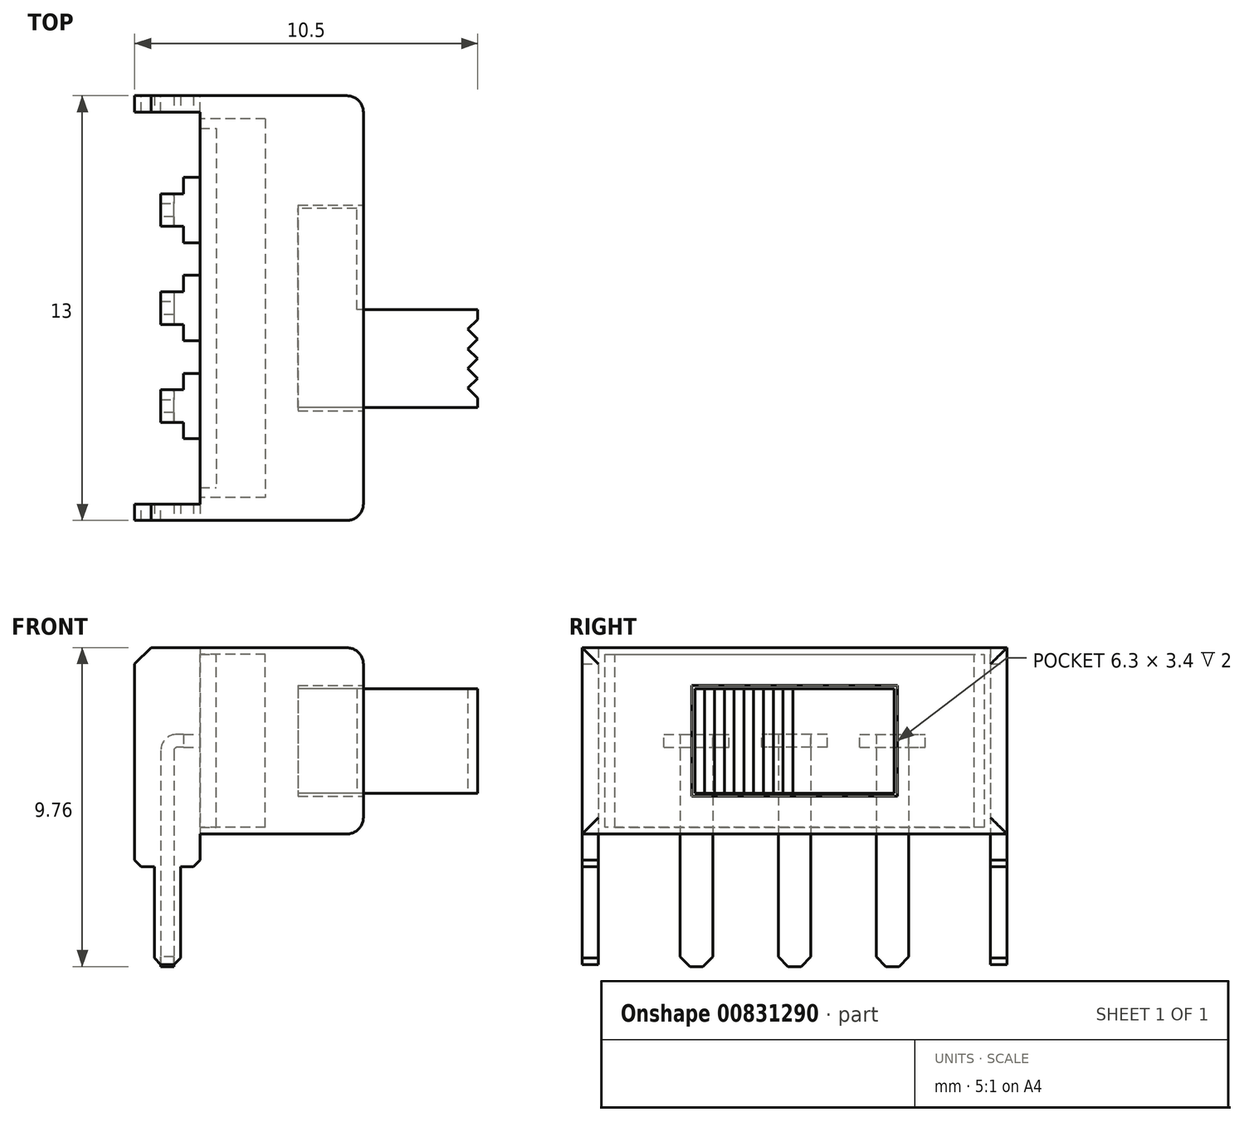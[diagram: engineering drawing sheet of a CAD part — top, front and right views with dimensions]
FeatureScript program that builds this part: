
annotation { "Feature Type Name" : "Feature", "Feature Type Description" : "" }
export const myFeature = defineFeature(function(context is Context, id is Id, definition is map)
    precondition{}
    {
        {
            var Q0;
            Q0=qCreatedBy(makeId("Top.planeOp"),FACE);
            var sketch = newSketch(context, id + "F0", { "sketchPlane" : qUnion([Q0])});
            skLineSegment(sketch, "E0.bottom", {"start": v(2.5, 6.5) * mm, "end": v(-2.5, 6.5) * mm});
            skLineSegment(sketch, "E0.top", {"start": v(2.5, -6.5) * mm, "end": v(-2.5, -6.5) * mm});
            skLineSegment(sketch, "E0.left", {"start": v(2.5, 6.5) * mm, "end": v(2.5, -6.5) * mm});
            skLineSegment(sketch, "E0.right", {"start": v(-2.5, 6.5) * mm, "end": v(-2.5, -6.5) * mm});
            skPoint(sketch, "E0.middle", {"position": v(0, 0) * mm});
            skSolve(sketch);
        }
        {
            var Q0;
            Q0 = qSketchRegion(id + "F0", true);
            extrude(context, id + "F1", {"entities" : qUnion([Q0]), "depth" : 5.7 * mm, "offsetDistance" : 25 * mm});
        }
        {
            var Q0;
            Q0=makeQuery(id+"F1.opExtrude","SWEPT_FACE",FACE,{"disambiguationData":[OSD([sQuery(id+"F0.wireOp",EDGE,"E0.left")])]});
            var sketch = newSketch(context, id + "F2", { "sketchPlane" : qUnion([Q0])});
            skLineSegment(sketch, "E1.bottom", {"start": v(3.15, 4.55) * mm, "end": v(-3.15, 4.55) * mm});
            skLineSegment(sketch, "E1.top", {"start": v(3.15, 1.15) * mm, "end": v(-3.15, 1.15) * mm});
            skLineSegment(sketch, "E1.left", {"start": v(3.15, 4.55) * mm, "end": v(3.15, 1.15) * mm});
            skLineSegment(sketch, "E1.right", {"start": v(-3.15, 4.55) * mm, "end": v(-3.15, 1.15) * mm});
            skPoint(sketch, "E1.middle", {"position": v(0, 2.85) * mm});
            skPoint(sketch, "E1.middle.positionSnap0", {"position": v(-6.5, 2.85) * mm});
            skPoint(sketch, "E1.middle.positionSnap1", {"position": v(0, 5.7) * mm});
            skPoint(sketch, "E1.centerSnap0", {"position": v(-6.5, 2.85) * mm});
            skPoint(sketch, "E1.centerSnap1", {"position": v(0, 5.7) * mm});
            skSolve(sketch);
        }
        {
            var Q0;
            Q0 = qSketchRegion(id + "F2", true);
            extrude(context, id + "F3", {"entities" : qUnion([Q0]), "operationType" : NewBodyOperationType.REMOVE, "oppositeDirection" : true, "depth" : 2 * mm, "offsetDistance" : 25 * mm});
        }
        {
            var Q0;
            Q0=makeQuery(id+"F3.boolean.opBoolean","COPY",FACE,{"derivedFrom":makeQuery(id+"F3.opExtrude","CAP_FACE",FACE,{"disambiguationData":[OSD([sQuery(id+"F2.wireOp",EDGE,"E1.bottom"),sQuery(id+"F2.wireOp",EDGE,"E1.top"),sQuery(id+"F2.wireOp",EDGE,"E1.left"),sQuery(id+"F2.wireOp",EDGE,"E1.right")])],"isStart":false})});
            var sketch = newSketch(context, id + "F4", { "sketchPlane" : qUnion([Q0])});
            skLineSegment(sketch, "E2.0", {"start": v(-3.05, 1.25) * mm, "end": v(3.05, 1.25) * mm});
            skLineSegment(sketch, "E2.1", {"start": v(-3.05, 4.45) * mm, "end": v(-3.05, 1.25) * mm});
            skLineSegment(sketch, "E2.2", {"start": v(3.05, 4.45) * mm, "end": v(-3.05, 4.45) * mm});
            skLineSegment(sketch, "E2.3", {"start": v(3.05, 1.25) * mm, "end": v(3.05, 4.45) * mm});
            skSolve(sketch);
        }
        {
            var Q0;
            Q0=makeQuery(id+"F4.imprint","IMPRINT",FACE,{"disambiguationData":[TD([[makeQuery(id+"F4.imprint","IMPRINT",EDGE,{"derivedFrom":sQuery(id+"F4.wireOp",EDGE,"E2.0")}),1.0]])]});
            extrude(context, id + "F5", {"entities" : qUnion([Q0]), "depth" : 1.8 * mm, "offsetDistance" : 25 * mm});
        }
        {
            var Q0;
            Q0=makeQuery(id+"F5.opExtrude","CAP_FACE",FACE,{"disambiguationData":[OSD([sQuery(id+"F4.wireOp",EDGE,"E2.0"),sQuery(id+"F4.wireOp",EDGE,"E2.1"),sQuery(id+"F4.wireOp",EDGE,"E2.2"),sQuery(id+"F4.wireOp",EDGE,"E2.3")])],"isStart":false});
            var sketch = newSketch(context, id + "F6", { "sketchPlane" : qUnion([Q0])});
            skLineSegment(sketch, "E3", {"start": v(-0.05, 4.45) * mm, "end": v(-0.05, 1.25) * mm});
            skSolve(sketch);
        }
        {
            var Q0;
            Q0 = qSketchRegion(id + "F6", true);
            var Q1;
            {var subQ0=sQuery(id+"F6.wireOp",EDGE,"E3");Q1=makeQuery(id+"F6.imprint","IMPRINT",FACE,{"disambiguationData":[TD([[makeQuery(id+"F6.imprint","IMPRINT",EDGE,{"derivedFrom":subQ0}),-1.0]])]});}
            extrude(context, id + "F7", {"entities" : qUnion([Q0, Q1]), "operationType" : NewBodyOperationType.ADD, "depth" : 3.7 * mm, "offsetDistance" : 25 * mm});
        }
        {
            var Q0;
            Q0=makeQuery(id+"F1.opExtrude","SWEPT_FACE",FACE,{"disambiguationData":[OSD([sQuery(id+"F0.wireOp",EDGE,"E0.right")])]});
            var sketch = newSketch(context, id + "F8", { "sketchPlane" : qUnion([Q0])});
            skLineSegment(sketch, "E4", {"start": v(-6, 5.7) * mm, "end": v(-6, 0) * mm});
            skLineSegment(sketch, "E5", {"start": v(6, 5.7) * mm, "end": v(6, 0) * mm});
            skSolve(sketch);
        }
        {
            var Q0;
            Q0 = qSketchRegion(id + "F8", true);
            var Q1;
            {var subQ0=sQuery(id+"F8.wireOp",EDGE,"E4");Q1=makeQuery(id+"F8.imprint","IMPRINT",FACE,{"disambiguationData":[TD([[makeQuery(id+"F8.imprint","IMPRINT",EDGE,{"derivedFrom":subQ0}),-1.0]])]});}
            var Q2;
            {var subQ0=sQuery(id+"F8.wireOp",EDGE,"E5");Q2=makeQuery(id+"F8.imprint","IMPRINT",FACE,{"disambiguationData":[TD([[makeQuery(id+"F8.imprint","IMPRINT",EDGE,{"derivedFrom":subQ0}),1.0]])]});}
            extrude(context, id + "F9", {"entities" : qUnion([Q0, Q1, Q2]), "operationType" : NewBodyOperationType.ADD, "depth" : 2 * mm, "offsetDistance" : 25 * mm});
        }
        {
            var Q0;
            {var subQ0=sQuery(id+"F0.wireOp",EDGE,"E0.right");var subQ1=makeQuery(id+"F1.opExtrude","CAP_EDGE",EDGE,{"disambiguationData":[OSD([subQ0])],"isStart":true});var subQ2=sQuery(id+"F0.wireOp",EDGE,"E0.top");var subQ3=sQuery(id+"F0.wireOp",EDGE,"E0.bottom");Q0=makeQuery(id+"F9.boolean.opBoolean","MERGE",FACE,{"derivedFrom":[makeQuery(id+"F1.opExtrude","CAP_FACE",FACE,{"disambiguationData":[OSD([subQ3,subQ2,sQuery(id+"F0.wireOp",EDGE,"E0.left"),subQ0])],"isStart":true}),makeQuery(id+"F9.opExtrude","SWEPT_FACE",FACE,{"disambiguationData":[OSD([subQ0]),TDD([makeQuery(id+"F8.imprint","IMPRINT",EDGE,{"disambiguationData":[TD([[makeQuery(id+"F8.imprint","INTERSECT",VERTEX,{"derivedFrom":[subQ1,sQuery(id+"F8.wireOp",EDGE,"E4")]}),1.0]])],"derivedFrom":subQ1})])]}),makeQuery(id+"F9.opExtrude","SWEPT_FACE",FACE,{"disambiguationData":[OSD([subQ0]),TDD([makeQuery(id+"F8.imprint","IMPRINT",EDGE,{"disambiguationData":[TD([[makeQuery(id+"F8.imprint","INTERSECT",VERTEX,{"derivedFrom":[subQ1,sQuery(id+"F8.wireOp",EDGE,"E5")]}),-1.0]])],"derivedFrom":subQ1})])]})]});}
            var sketch = newSketch(context, id + "F10", { "sketchPlane" : qUnion([Q0])});
            skLineSegment(sketch, "E6", {"start": v(-2.5, -6) * mm, "end": v(-2.5, -6.5) * mm});
            skLineSegment(sketch, "E7", {"start": v(-2.5, 6) * mm, "end": v(-2.5, 6.5) * mm});
            skSolve(sketch);
        }
        {
            var Q0;
            Q0 = qSketchRegion(id + "F10", true);
            var Q1;
            {var subQ0=sQuery(id+"F10.wireOp",EDGE,"E7");Q1=makeQuery(id+"F10.imprint","IMPRINT",FACE,{"disambiguationData":[TD([[makeQuery(id+"F10.imprint","IMPRINT",EDGE,{"derivedFrom":subQ0}),1.0]])]});}
            var Q2;
            {var subQ0=sQuery(id+"F10.wireOp",EDGE,"E6");Q2=makeQuery(id+"F10.imprint","IMPRINT",FACE,{"disambiguationData":[TD([[makeQuery(id+"F10.imprint","IMPRINT",EDGE,{"derivedFrom":subQ0}),-1.0]])]});}
            extrude(context, id + "F11", {"entities" : qUnion([Q0, Q1, Q2]), "operationType" : NewBodyOperationType.ADD, "depth" : 1 * mm, "offsetDistance" : 25 * mm});
        }
        {
            var Q0;
            Q0=makeQuery(id+"F11.opExtrude","CAP_FACE",FACE,{"disambiguationData":[OSD([sQuery(id+"F0.wireOp",EDGE,"E0.bottom"),sQuery(id+"F0.wireOp",EDGE,"E0.right"),sQuery(id+"F8.wireOp",EDGE,"E4"),sQuery(id+"F10.wireOp",EDGE,"E6")])],"isStart":false});
            var sketch = newSketch(context, id + "F12", { "sketchPlane" : qUnion([Q0])});
            skLineSegment(sketch, "E8", {"start": v(-3.1, -6.5) * mm, "end": v(-3.1, -6) * mm});
            skLineSegment(sketch, "E9", {"start": v(-3.9, -6.5) * mm, "end": v(-3.9, -6) * mm});
            skSolve(sketch);
        }
        {
            var Q0;
            Q0 = qSketchRegion(id + "F12", true);
            var Q1;
            {var subQ0=sQuery(id+"F12.wireOp",EDGE,"E8");Q1=makeQuery(id+"F12.imprint","IMPRINT",FACE,{"disambiguationData":[TD([[makeQuery(id+"F12.imprint","IMPRINT",EDGE,{"derivedFrom":subQ0}),1.0]])]});}
            extrude(context, id + "F13", {"entities" : qUnion([Q0, Q1]), "operationType" : NewBodyOperationType.ADD, "depth" : 3 * mm, "offsetDistance" : 25 * mm});
        }
        {
            var Q0;
            Q0=makeQuery(id+"F11.opExtrude","CAP_FACE",FACE,{"disambiguationData":[OSD([sQuery(id+"F0.wireOp",EDGE,"E0.top"),sQuery(id+"F0.wireOp",EDGE,"E0.right"),sQuery(id+"F8.wireOp",EDGE,"E5"),sQuery(id+"F10.wireOp",EDGE,"E7")])],"isStart":false});
            var sketch = newSketch(context, id + "F14", { "sketchPlane" : qUnion([Q0])});
            skLineSegment(sketch, "E10", {"start": v(-3.1, 6) * mm, "end": v(-3.1, 6.5) * mm});
            skLineSegment(sketch, "E11", {"start": v(-3.9, 6) * mm, "end": v(-3.9, 6.5) * mm});
            skSolve(sketch);
        }
        {
            var Q0;
            Q0 = qSketchRegion(id + "F14", true);
            var Q1;
            {var subQ0=sQuery(id+"F14.wireOp",EDGE,"E10");Q1=makeQuery(id+"F14.imprint","IMPRINT",FACE,{"disambiguationData":[TD([[makeQuery(id+"F14.imprint","IMPRINT",EDGE,{"derivedFrom":subQ0}),1.0]])]});}
            extrude(context, id + "F15", {"entities" : qUnion([Q0, Q1]), "operationType" : NewBodyOperationType.ADD, "depth" : 3 * mm, "offsetDistance" : 25 * mm});
        }
        {
            var Q0;
            Q0=makeQuery(id+"F13.opExtrude","CAP_EDGE",EDGE,{"disambiguationData":[OSD([sQuery(id+"F12.wireOp",EDGE,"E9")])],"isStart":false});
            var Q1;
            Q1=makeQuery(id+"F13.opExtrude","CAP_EDGE",EDGE,{"disambiguationData":[OSD([sQuery(id+"F12.wireOp",EDGE,"E8")])],"isStart":false});
            var Q2;
            Q2=makeQuery(id+"F15.opExtrude","CAP_EDGE",EDGE,{"disambiguationData":[OSD([sQuery(id+"F14.wireOp",EDGE,"E11")])],"isStart":false});
            var Q3;
            Q3=makeQuery(id+"F15.opExtrude","CAP_EDGE",EDGE,{"disambiguationData":[OSD([sQuery(id+"F14.wireOp",EDGE,"E10")])],"isStart":false});
            chamfer(context, id + "F16", {"entities" : qUnion([Q0, Q1, Q2, Q3]), "width" : 0.2 * mm, "tangentPropagation" : true});
        }
        {
            var Q0;
            {var subQ0=sQuery(id+"F0.wireOp",EDGE,"E0.right");var subQ1=makeQuery(id+"F1.opExtrude","CAP_EDGE",EDGE,{"disambiguationData":[OSD([subQ0])],"isStart":true});Q0=makeQuery(id+"F11.opExtrude","CAP_EDGE",EDGE,{"disambiguationData":[OSD([subQ0]),TDD([makeQuery(id+"F10.imprint","IMPRINT",EDGE,{"derivedFrom":makeQuery(id+"F9.opExtrude","CAP_EDGE",EDGE,{"disambiguationData":[OSD([subQ0]),TDD([makeQuery(id+"F8.imprint","IMPRINT",EDGE,{"disambiguationData":[TD([[makeQuery(id+"F8.imprint","INTERSECT",VERTEX,{"derivedFrom":[subQ1,sQuery(id+"F8.wireOp",EDGE,"E4")]}),1.0]])],"derivedFrom":subQ1})])],"isStart":false})})])],"isStart":false});}
            var Q1;
            Q1=makeQuery(id+"F11.opExtrude","CAP_EDGE",EDGE,{"disambiguationData":[OSD([sQuery(id+"F10.wireOp",EDGE,"E6")])],"isStart":false});
            var Q2;
            {var subQ0=sQuery(id+"F0.wireOp",EDGE,"E0.right");var subQ1=makeQuery(id+"F1.opExtrude","CAP_EDGE",EDGE,{"disambiguationData":[OSD([subQ0])],"isStart":true});Q2=makeQuery(id+"F11.opExtrude","CAP_EDGE",EDGE,{"disambiguationData":[OSD([subQ0]),TDD([makeQuery(id+"F10.imprint","IMPRINT",EDGE,{"derivedFrom":makeQuery(id+"F9.opExtrude","CAP_EDGE",EDGE,{"disambiguationData":[OSD([subQ0]),TDD([makeQuery(id+"F8.imprint","IMPRINT",EDGE,{"disambiguationData":[TD([[makeQuery(id+"F8.imprint","INTERSECT",VERTEX,{"derivedFrom":[subQ1,sQuery(id+"F8.wireOp",EDGE,"E5")]}),-1.0]])],"derivedFrom":subQ1})])],"isStart":false})})])],"isStart":false});}
            var Q3;
            Q3=makeQuery(id+"F11.opExtrude","CAP_EDGE",EDGE,{"disambiguationData":[OSD([sQuery(id+"F10.wireOp",EDGE,"E7")])],"isStart":false});
            chamfer(context, id + "F17", {"entities" : qUnion([Q0, Q1, Q2, Q3]), "width" : 0.2 * mm, "tangentPropagation" : true});
        }
        {
            var Q0;
            Q0=makeQuery(id+"F1.opExtrude","CAP_EDGE",EDGE,{"disambiguationData":[OSD([sQuery(id+"F0.wireOp",EDGE,"E0.left")])],"isStart":false});
            var Q1;
            Q1=makeQuery(id+"F1.opExtrude","SWEPT_EDGE",EDGE,{"disambiguationData":[OSD([sQuery(id+"F0.wireOp",EDGE,"E0.bottom"),sQuery(id+"F0.wireOp",EDGE,"E0.left")])]});
            var Q2;
            Q2=makeQuery(id+"F1.opExtrude","CAP_EDGE",EDGE,{"disambiguationData":[OSD([sQuery(id+"F0.wireOp",EDGE,"E0.left")])],"isStart":true});
            var Q3;
            Q3=makeQuery(id+"F1.opExtrude","SWEPT_EDGE",EDGE,{"disambiguationData":[OSD([sQuery(id+"F0.wireOp",EDGE,"E0.top"),sQuery(id+"F0.wireOp",EDGE,"E0.left")])]});
            fillet(context, id + "F18", {"entities" : qUnion([Q0, Q1, Q2, Q3]), "radius" : 0.5 * mm, "tangentPropagation" : true, "allowEdgeOverflow" : false});
        }
        {
            var Q0;
            {var subQ0=sQuery(id+"F0.wireOp",EDGE,"E0.right");var subQ1=makeQuery(id+"F1.opExtrude","CAP_EDGE",EDGE,{"disambiguationData":[OSD([subQ0])],"isStart":false});Q0=makeQuery(id+"F9.opExtrude","CAP_EDGE",EDGE,{"disambiguationData":[OSD([subQ0]),TDD([makeQuery(id+"F8.imprint","IMPRINT",EDGE,{"disambiguationData":[TD([[makeQuery(id+"F8.imprint","INTERSECT",VERTEX,{"derivedFrom":[subQ1,sQuery(id+"F8.wireOp",EDGE,"E4")]}),1.0]])],"derivedFrom":subQ1})])],"isStart":false});}
            var Q1;
            {var subQ0=sQuery(id+"F0.wireOp",EDGE,"E0.right");var subQ1=makeQuery(id+"F1.opExtrude","CAP_EDGE",EDGE,{"disambiguationData":[OSD([subQ0])],"isStart":false});Q1=makeQuery(id+"F9.opExtrude","CAP_EDGE",EDGE,{"disambiguationData":[OSD([subQ0]),TDD([makeQuery(id+"F8.imprint","IMPRINT",EDGE,{"disambiguationData":[TD([[makeQuery(id+"F8.imprint","INTERSECT",VERTEX,{"derivedFrom":[subQ1,sQuery(id+"F8.wireOp",EDGE,"E5")]}),-1.0]])],"derivedFrom":subQ1})])],"isStart":false});}
            chamfer(context, id + "F19", {"entities" : qUnion([Q0, Q1]), "width" : 0.5 * mm, "tangentPropagation" : true});
        }
        {
            var Q0;
            Q0=makeQuery(id+"F1.opExtrude","SWEPT_FACE",FACE,{"disambiguationData":[OSD([sQuery(id+"F0.wireOp",EDGE,"E0.right")])]});
            var sketch = newSketch(context, id + "F20", { "sketchPlane" : qUnion([Q0])});
            skLineSegment(sketch, "E12.0", {"start": v(5.8, 0.2) * mm, "end": v(5.8, 5.5) * mm});
            skLineSegment(sketch, "E12.1", {"start": v(-5.8, 0.2) * mm, "end": v(5.8, 0.2) * mm});
            skLineSegment(sketch, "E12.2", {"start": v(-5.8, 5.5) * mm, "end": v(-5.8, 0.2) * mm});
            skLineSegment(sketch, "E12.3", {"start": v(5.8, 5.5) * mm, "end": v(-5.8, 5.5) * mm});
            skSolve(sketch);
        }
        {
            var Q0;
            Q0 = qSketchRegion(id + "F20", true);
            extrude(context, id + "F21", {"entities" : qUnion([Q0]), "operationType" : NewBodyOperationType.REMOVE, "oppositeDirection" : true, "depth" : 2 * mm, "offsetDistance" : 25 * mm});
        }
        {
            var Q0;
            Q0=makeQuery(id+"F21.boolean.opBoolean","COPY",FACE,{"derivedFrom":makeQuery(id+"F21.opExtrude","SWEPT_FACE",FACE,{"disambiguationData":[OSD([sQuery(id+"F20.wireOp",EDGE,"E12.3")])]})});
            var sketch = newSketch(context, id + "F22", { "sketchPlane" : qUnion([Q0])});
            skLineSegment(sketch, "E13.bottom", {"start": v(-2.5, -5.5) * mm, "end": v(-2, -5.5) * mm});
            skLineSegment(sketch, "E13.top", {"start": v(-2.5, 5.5) * mm, "end": v(-2, 5.5) * mm});
            skLineSegment(sketch, "E13.left", {"start": v(-2.5, -5.5) * mm, "end": v(-2.5, 5.5) * mm});
            skLineSegment(sketch, "E13.right", {"start": v(-2, -5.5) * mm, "end": v(-2, 5.5) * mm});
            skSolve(sketch);
        }
        {
            var Q0;
            Q0 = qSketchRegion(id + "F22", true);
            extrude(context, id + "F23", {"entities" : qUnion([Q0]), "depth" : 5.3 * mm, "offsetDistance" : 25 * mm});
        }
        {
            var Q0;
            Q0=makeQuery(id+"F23.opExtrude","SWEPT_FACE",FACE,{"disambiguationData":[OSD([sQuery(id+"F22.wireOp",EDGE,"E13.left")])]});
            var sketch = newSketch(context, id + "F24", { "sketchPlane" : qUnion([Q0])});
            skLineSegment(sketch, "E14.bottom", {"start": v(-2, 2.65) * mm, "end": v(-4, 2.65) * mm});
            skLineSegment(sketch, "E14.top", {"start": v(-2, 3.05) * mm, "end": v(-4, 3.05) * mm});
            skLineSegment(sketch, "E14.left", {"start": v(-2, 2.65) * mm, "end": v(-2, 3.05) * mm});
            skLineSegment(sketch, "E14.right", {"start": v(-4, 2.65) * mm, "end": v(-4, 3.05) * mm});
            skPoint(sketch, "E14.middle", {"position": v(-3, 2.85) * mm});
            skPoint(sketch, "E14.middle.positionSnap0", {"position": v(-5.5, 2.85) * mm});
            skPoint(sketch, "E14.centerSnap0", {"position": v(-5.5, 2.85) * mm});
            skLineSegment(sketch, "E15.bottom", {"start": v(-1, 2.65) * mm, "end": v(1, 2.65) * mm});
            skLineSegment(sketch, "E15.top", {"start": v(-1, 3.05) * mm, "end": v(1, 3.05) * mm});
            skLineSegment(sketch, "E15.left", {"start": v(-1, 2.65) * mm, "end": v(-1, 3.05) * mm});
            skLineSegment(sketch, "E15.right", {"start": v(1, 2.65) * mm, "end": v(1, 3.05) * mm});
            skPoint(sketch, "E15.middle", {"position": v(0, 2.85) * mm});
            skPoint(sketch, "E15.middle.positionSnap0", {"position": v(-2, 2.85) * mm});
            skPoint(sketch, "E15.middle.positionSnap1", {"position": v(0, 5.5) * mm});
            skPoint(sketch, "E15.centerSnap0", {"position": v(-2, 2.85) * mm});
            skPoint(sketch, "E15.centerSnap1", {"position": v(0, 5.5) * mm});
            skLineSegment(sketch, "E16.bottom", {"start": v(4, 2.65) * mm, "end": v(2, 2.65) * mm});
            skLineSegment(sketch, "E16.top", {"start": v(4, 3.05) * mm, "end": v(2, 3.05) * mm});
            skLineSegment(sketch, "E16.left", {"start": v(4, 2.65) * mm, "end": v(4, 3.05) * mm});
            skLineSegment(sketch, "E16.right", {"start": v(2, 2.65) * mm, "end": v(2, 3.05) * mm});
            skPoint(sketch, "E16.middle", {"position": v(3, 2.85) * mm});
            skSolve(sketch);
        }
        {
            var Q0;
            Q0=makeQuery(id+"F24.imprint","IMPRINT",FACE,{"disambiguationData":[TD([[makeQuery(id+"F24.imprint","IMPRINT",EDGE,{"derivedFrom":sQuery(id+"F24.wireOp",EDGE,"E15.bottom")}),1.0]])]});
            var Q1;
            Q1=makeQuery(id+"F24.imprint","IMPRINT",FACE,{"disambiguationData":[TD([[makeQuery(id+"F24.imprint","IMPRINT",EDGE,{"derivedFrom":sQuery(id+"F24.wireOp",EDGE,"E16.bottom")}),-1.0]])]});
            var Q2;
            Q2=makeQuery(id+"F24.imprint","IMPRINT",FACE,{"disambiguationData":[TD([[makeQuery(id+"F24.imprint","IMPRINT",EDGE,{"derivedFrom":sQuery(id+"F24.wireOp",EDGE,"E14.bottom")}),-1.0]])]});
            extrude(context, id + "F25", {"entities" : qUnion([Q0, Q1, Q2]), "depth" : 0.5 * mm, "offsetDistance" : 25 * mm});
        }
        {
            var Q0;
            Q0=makeQuery(id+"F25.opExtrude","CAP_FACE",FACE,{"disambiguationData":[OSD([sQuery(id+"F24.wireOp",EDGE,"E15.bottom"),sQuery(id+"F24.wireOp",EDGE,"E15.top"),sQuery(id+"F24.wireOp",EDGE,"E15.left"),sQuery(id+"F24.wireOp",EDGE,"E15.right")])],"isStart":false});
            var sketch = newSketch(context, id + "F26", { "sketchPlane" : qUnion([Q0])});
            skLineSegment(sketch, "E17", {"start": v(0.5, 3.05) * mm, "end": v(0.5, 2.65) * mm});
            skLineSegment(sketch, "E18", {"start": v(-0.5, 2.65) * mm, "end": v(-0.5, 3.05) * mm});
            skSolve(sketch);
        }
        {
            var Q0;
            Q0=makeQuery(id+"F25.opExtrude","SWEPT_FACE",FACE,{"disambiguationData":[OSD([sQuery(id+"F24.wireOp",EDGE,"E15.left")])]});
            var sketch = newSketch(context, id + "F27", { "sketchPlane" : qUnion([Q0])});
            skLineSegment(sketch, "E19", {"start": v(3.5, -4.06) * mm, "end": v(3.5, 2.55) * mm});
            skLineSegment(sketch, "E20", {"start": v(3.2, 2.85) * mm, "end": v(3, 2.85) * mm});
            skPoint(sketch, "E21.visualSharp", {"position": v(3.5, 2.85) * mm});
            skArc(sketch, "E21.filletArc", {"start": v(3.5, 2.55) * mm, "mid": v(3.41, 2.76) * mm, "end": v(3.2, 2.85) * mm});
            skSolve(sketch);
        }
        {
            var Q0;
            {var subQ0=sQuery(id+"F26.wireOp",EDGE,"E17");Q0=makeQuery(id+"F26.imprint","IMPRINT",FACE,{"disambiguationData":[TD([[makeQuery(id+"F26.imprint","IMPRINT",EDGE,{"derivedFrom":subQ0}),-1.0]])]});}
            var Q1;
            Q1=sQuery(id+"F27.wireOp",EDGE,"E19");
            var Q2;
            Q2=sQuery(id+"F27.wireOp",EDGE,"E21.filletArc");
            var Q3;
            Q3=sQuery(id+"F27.wireOp",EDGE,"E20");
            sweep(context, id + "F28", {"operationType" : NewBodyOperationType.ADD, "profiles" : qUnion([Q0]), "path" : qUnion([Q1, Q2, Q3])});
        }
        {
            var Q0;
            Q0=makeQuery(id+"F25.opExtrude","CAP_FACE",FACE,{"disambiguationData":[OSD([sQuery(id+"F24.wireOp",EDGE,"E16.bottom"),sQuery(id+"F24.wireOp",EDGE,"E16.top"),sQuery(id+"F24.wireOp",EDGE,"E16.left"),sQuery(id+"F24.wireOp",EDGE,"E16.right")])],"isStart":false});
            var sketch = newSketch(context, id + "F29", { "sketchPlane" : qUnion([Q0])});
            skLineSegment(sketch, "E22", {"start": v(3.5, 3.05) * mm, "end": v(3.5, 2.65) * mm});
            skLineSegment(sketch, "E23", {"start": v(2.5, 2.65) * mm, "end": v(2.5, 3.05) * mm});
            skSolve(sketch);
        }
        {
            var Q0;
            {var subQ0=sQuery(id+"F29.wireOp",EDGE,"E22");Q0=makeQuery(id+"F29.imprint","IMPRINT",FACE,{"disambiguationData":[TD([[makeQuery(id+"F29.imprint","IMPRINT",EDGE,{"derivedFrom":subQ0}),-1.0]])]});}
            var Q1;
            Q1=sQuery(id+"F27.wireOp",EDGE,"E20");
            var Q2;
            Q2=sQuery(id+"F27.wireOp",EDGE,"E21.filletArc");
            var Q3;
            Q3=sQuery(id+"F27.wireOp",EDGE,"E19");
            sweep(context, id + "F30", {"operationType" : NewBodyOperationType.ADD, "profiles" : qUnion([Q0]), "path" : qUnion([Q1, Q2, Q3])});
        }
        {
            var Q0;
            Q0=makeQuery(id+"F25.opExtrude","CAP_FACE",FACE,{"disambiguationData":[OSD([sQuery(id+"F24.wireOp",EDGE,"E14.bottom"),sQuery(id+"F24.wireOp",EDGE,"E14.top"),sQuery(id+"F24.wireOp",EDGE,"E14.left"),sQuery(id+"F24.wireOp",EDGE,"E14.right")])],"isStart":false});
            var sketch = newSketch(context, id + "F31", { "sketchPlane" : qUnion([Q0])});
            skLineSegment(sketch, "E24", {"start": v(-2.5, 3.05) * mm, "end": v(-2.5, 2.65) * mm});
            skLineSegment(sketch, "E25", {"start": v(-3.5, 2.65) * mm, "end": v(-3.5, 3.05) * mm});
            skSolve(sketch);
        }
        {
            var Q0;
            {var subQ0=sQuery(id+"F31.wireOp",EDGE,"E24");Q0=makeQuery(id+"F31.imprint","IMPRINT",FACE,{"disambiguationData":[TD([[makeQuery(id+"F31.imprint","IMPRINT",EDGE,{"derivedFrom":subQ0}),-1.0]])]});}
            var Q1;
            Q1=sQuery(id+"F27.wireOp",EDGE,"E20");
            var Q2;
            Q2=sQuery(id+"F27.wireOp",EDGE,"E21.filletArc");
            var Q3;
            Q3=sQuery(id+"F27.wireOp",EDGE,"E19");
            sweep(context, id + "F32", {"operationType" : NewBodyOperationType.ADD, "profiles" : qUnion([Q0]), "path" : qUnion([Q1, Q2, Q3])});
        }
        {
            var Q0;
            Q0=makeQuery(id+"F30.opSweep","CAP_EDGE",EDGE,{"disambiguationData":[OSD([sQuery(id+"F27.wireOp",VERTEX,"E19.start"),sQuery(id+"F29.wireOp",EDGE,"E22")])],"isStart":false});
            var Q1;
            Q1=makeQuery(id+"F30.opSweep","CAP_EDGE",EDGE,{"disambiguationData":[OSD([sQuery(id+"F27.wireOp",VERTEX,"E19.start"),sQuery(id+"F29.wireOp",EDGE,"E23")])],"isStart":false});
            var Q2;
            Q2=makeQuery(id+"F28.opSweep","CAP_EDGE",EDGE,{"disambiguationData":[OSD([sQuery(id+"F26.wireOp",EDGE,"E17"),sQuery(id+"F27.wireOp",VERTEX,"E19.start")])],"isStart":false});
            var Q3;
            Q3=makeQuery(id+"F28.opSweep","CAP_EDGE",EDGE,{"disambiguationData":[OSD([sQuery(id+"F26.wireOp",EDGE,"E18"),sQuery(id+"F27.wireOp",VERTEX,"E19.start")])],"isStart":false});
            var Q4;
            Q4=makeQuery(id+"F32.opSweep","CAP_EDGE",EDGE,{"disambiguationData":[OSD([sQuery(id+"F27.wireOp",VERTEX,"E19.start"),sQuery(id+"F31.wireOp",EDGE,"E24")])],"isStart":false});
            var Q5;
            Q5=makeQuery(id+"F32.opSweep","CAP_EDGE",EDGE,{"disambiguationData":[OSD([sQuery(id+"F27.wireOp",VERTEX,"E19.start"),sQuery(id+"F31.wireOp",EDGE,"E25")])],"isStart":false});
            chamfer(context, id + "F33", {"entities" : qUnion([Q0, Q1, Q2, Q3, Q4, Q5]), "width" : 0.3 * mm, "tangentPropagation" : true});
        }
        {
            var Q0;
            {var subQ0=sQuery(id+"F4.wireOp",EDGE,"E2.0");Q0=makeQuery(id+"F7.boolean.opBoolean","MERGE",FACE,{"derivedFrom":[makeQuery(id+"F5.opExtrude","SWEPT_FACE",FACE,{"disambiguationData":[OSD([subQ0])]}),makeQuery(id+"F7.opExtrude","SWEPT_FACE",FACE,{"disambiguationData":[OSD([subQ0])]})]});}
            var sketch = newSketch(context, id + "F34", { "sketchPlane" : qUnion([Q0])});
            skLineSegment(sketch, "E26", {"start": v(6, 3.05) * mm, "end": v(6, 2.75) * mm});
            skLineSegment(sketch, "E27", {"start": v(6, 2.75) * mm, "end": v(5.7, 2.45) * mm});
            skLineSegment(sketch, "E28", {"start": v(5.7, 2.45) * mm, "end": v(6, 2.15) * mm});
            skLineSegment(sketch, "E29", {"start": v(6, 2.15) * mm, "end": v(5.7, 1.85) * mm});
            skLineSegment(sketch, "E30", {"start": v(5.7, 1.85) * mm, "end": v(6, 1.55) * mm});
            skLineSegment(sketch, "E31", {"start": v(6, 1.55) * mm, "end": v(5.7, 1.25) * mm});
            skLineSegment(sketch, "E32", {"start": v(5.7, 1.25) * mm, "end": v(6, 0.95) * mm});
            skLineSegment(sketch, "E33", {"start": v(6, 0.95) * mm, "end": v(5.7, 0.65) * mm});
            skLineSegment(sketch, "E34", {"start": v(5.7, 0.65) * mm, "end": v(6, 0.35) * mm});
            skLineSegment(sketch, "E35", {"start": v(6, 0.35) * mm, "end": v(6, 0.05) * mm});
            skSolve(sketch);
        }
        {
            var Q0;
            {var subQ0=sQuery(id+"F34.wireOp",EDGE,"E27");Q0=makeQuery(id+"F34.imprint","IMPRINT",FACE,{"disambiguationData":[TD([[makeQuery(id+"F34.imprint","IMPRINT",EDGE,{"derivedFrom":subQ0}),1.0]])]});}
            var Q1;
            {var subQ0=sQuery(id+"F34.wireOp",EDGE,"E29");Q1=makeQuery(id+"F34.imprint","IMPRINT",FACE,{"disambiguationData":[TD([[makeQuery(id+"F34.imprint","IMPRINT",EDGE,{"derivedFrom":subQ0}),1.0]])]});}
            var Q2;
            {var subQ0=sQuery(id+"F34.wireOp",EDGE,"E31");Q2=makeQuery(id+"F34.imprint","IMPRINT",FACE,{"disambiguationData":[TD([[makeQuery(id+"F34.imprint","IMPRINT",EDGE,{"derivedFrom":subQ0}),1.0]])]});}
            var Q3;
            {var subQ0=sQuery(id+"F34.wireOp",EDGE,"E33");Q3=makeQuery(id+"F34.imprint","IMPRINT",FACE,{"disambiguationData":[TD([[makeQuery(id+"F34.imprint","IMPRINT",EDGE,{"derivedFrom":subQ0}),1.0]])]});}
            extrude(context, id + "F35", {"entities" : qUnion([Q0, Q1, Q2, Q3]), "operationType" : NewBodyOperationType.REMOVE, "oppositeDirection" : true, "depth" : 25 * mm, "offsetDistance" : 25 * mm});
        }
    });
